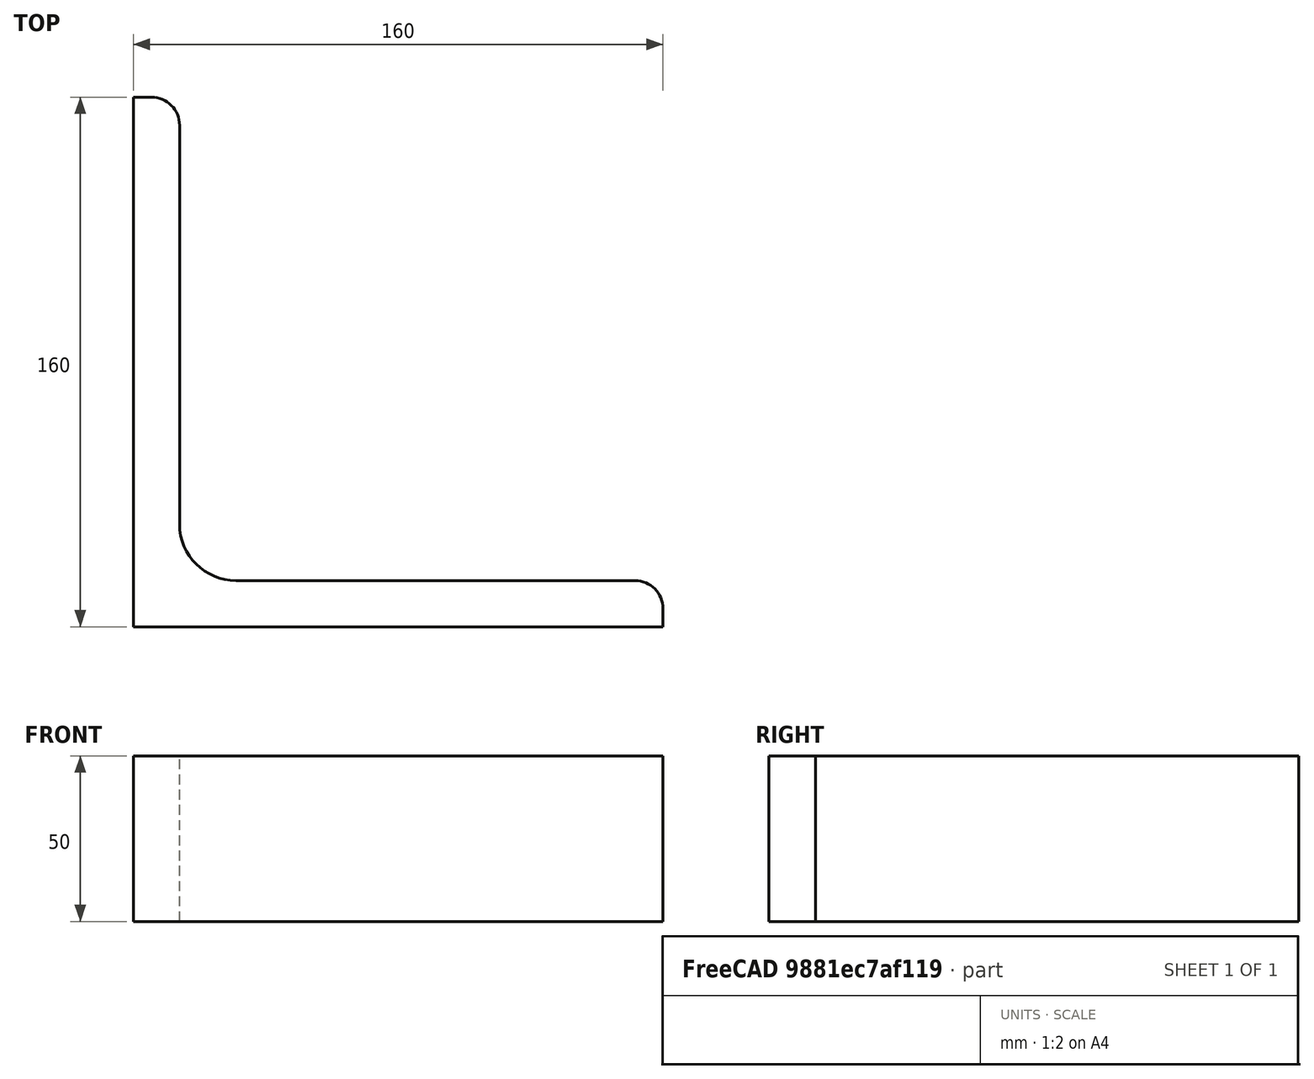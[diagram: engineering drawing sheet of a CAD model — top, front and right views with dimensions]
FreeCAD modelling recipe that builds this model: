
FCSTD DOCUMENT  (FreeCAD 0.15R4671 (Git))
Label: Angle Bar L160x160x14 EN10056 S235JR
License: All rights reserved
LicenseURL: http://en.wikipedia.org/wiki/All_rights_reserved
objects: Sketcher::SketchObject×1, Part::Extrusion×1
note: 2 computed .brp shape members not serialized (recipe doc carries the construction recipe); baked Part::Feature solids carry a one-line shape summary decoded from their .brp

FEATURE [Sketcher::SketchObject] Sketch
  sketch-geometry (9):
    g0: LineSegment StartX=0 StartY=0 StartZ=0 EndX=160 EndY=0 EndZ=0
    g1: LineSegment StartX=160 StartY=0 StartZ=0 EndX=160 EndY=5.5 EndZ=0
    g2: LineSegment StartX=151.5 StartY=14 StartZ=0 EndX=31 EndY=14 EndZ=0
    g3: LineSegment StartX=0 StartY=0 StartZ=0 EndX=0 EndY=160 EndZ=0
    g4: LineSegment StartX=0 StartY=160 StartZ=0 EndX=5.5 EndY=160 EndZ=0
    g5: LineSegment StartX=14 StartY=151.5 StartZ=0 EndX=14 EndY=31 EndZ=0
    g6: ArcOfCircle CenterX=31 CenterY=31 CenterZ=0 NormalX=0 NormalY=0 NormalZ=1 Radius=17 StartAngle=3.14159 EndAngle=4.71239
    g7: ArcOfCircle CenterX=5.5 CenterY=151.5 CenterZ=0 NormalX=0 NormalY=0 NormalZ=1 Radius=8.5 StartAngle=0 EndAngle=1.5708
    g8: ArcOfCircle CenterX=151.5 CenterY=5.5 CenterZ=0 NormalX=0 NormalY=0 NormalZ=1 Radius=8.5 StartAngle=0 EndAngle=1.5708
  constraints (23):
    c: Coincident(g0,g-1)
    c: Horizontal(g0)
    c: Coincident(g1,g0)
    c: Vertical(g1)
    c: Horizontal(g2)
    c: Coincident(g3,g-1)
    c: Vertical(g3)
    c: Coincident(g4,g3)
    c: Horizontal(g4)
    c: Vertical(g5)
    c: Tangent(g5,g6) = -1.5708
    c: Tangent(g2,g6) = 1.5708
    c: Tangent(g4,g7) = 1.5708
    c: Tangent(g5,g7) = 1.5708
    c: Tangent(g2,g8) = -1.5708
    c: Tangent(g1,g8) = -1.5708
    c: DistanceX(g0) = 160
    c: DistanceY(g3) = 160
    c: DistanceY(g0,g2) = 14
    c: DistanceX(g3,g5) = 14
    c: Radius(g6) = 17
    c: Radius(g8) = 8.5
    c: Radius(g7) = 8.5
FEATURE [Part::Extrusion] Extrude  label="Angle Bar L160x160x14 EN10056 S235JR"
  Base = -> Sketch
  Dir = (0,0,50)
  Solid = true
